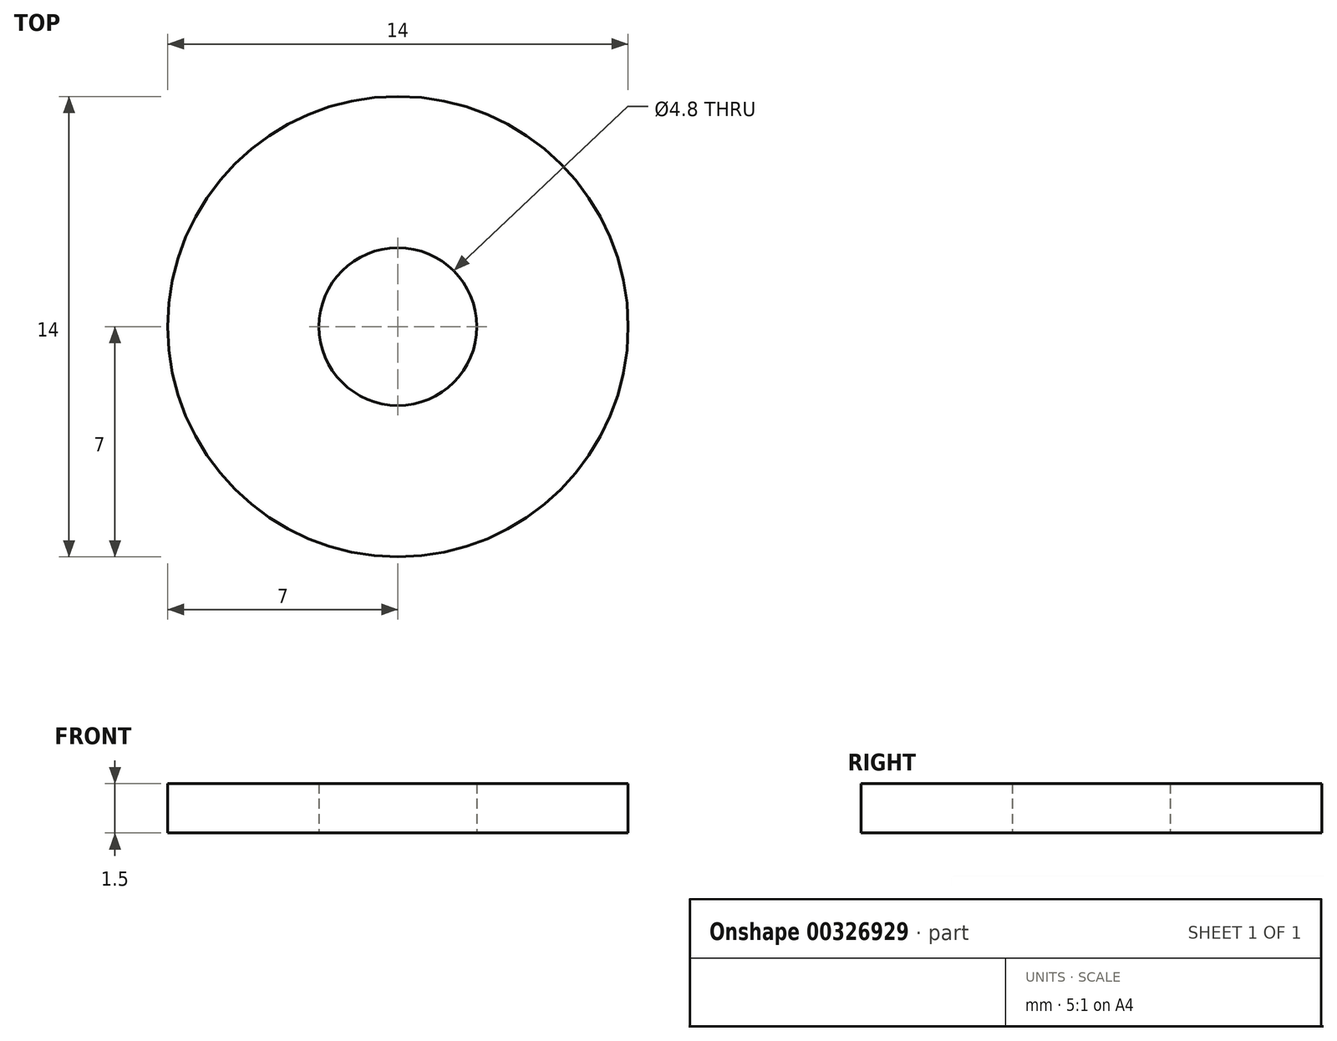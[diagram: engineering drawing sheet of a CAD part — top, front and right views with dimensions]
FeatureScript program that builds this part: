
annotation { "Feature Type Name" : "Feature", "Feature Type Description" : "" }
export const myFeature = defineFeature(function(context is Context, id is Id, definition is map)
    precondition{}
    {
        {
            var Q0;
            Q0=qCreatedBy(makeId("Top.planeOp"),FACE);
            var sketch = newSketch(context, id + "F0", { "sketchPlane" : qUnion([Q0])});
            skCircle(sketch, "E0", {"center": v(0, 0) * mm, "radius": 2.4 * mm});
            skCircle(sketch, "E1", {"center": v(0, 0) * mm, "radius": 7 * mm});
            skSolve(sketch);
        }
        {
            var Q0;
            Q0=makeQuery(id+"F0.imprint","IMPRINT",FACE,{"disambiguationData":[TD([[makeQuery(id+"F0.imprint","IMPRINT",EDGE,{"derivedFrom":sQuery(id+"F0.wireOp",EDGE,"E0")}),-1.0]])]});
            extrude(context, id + "F1", {"entities" : qUnion([Q0]), "depth" : 1.5 * mm});
        }
    });
